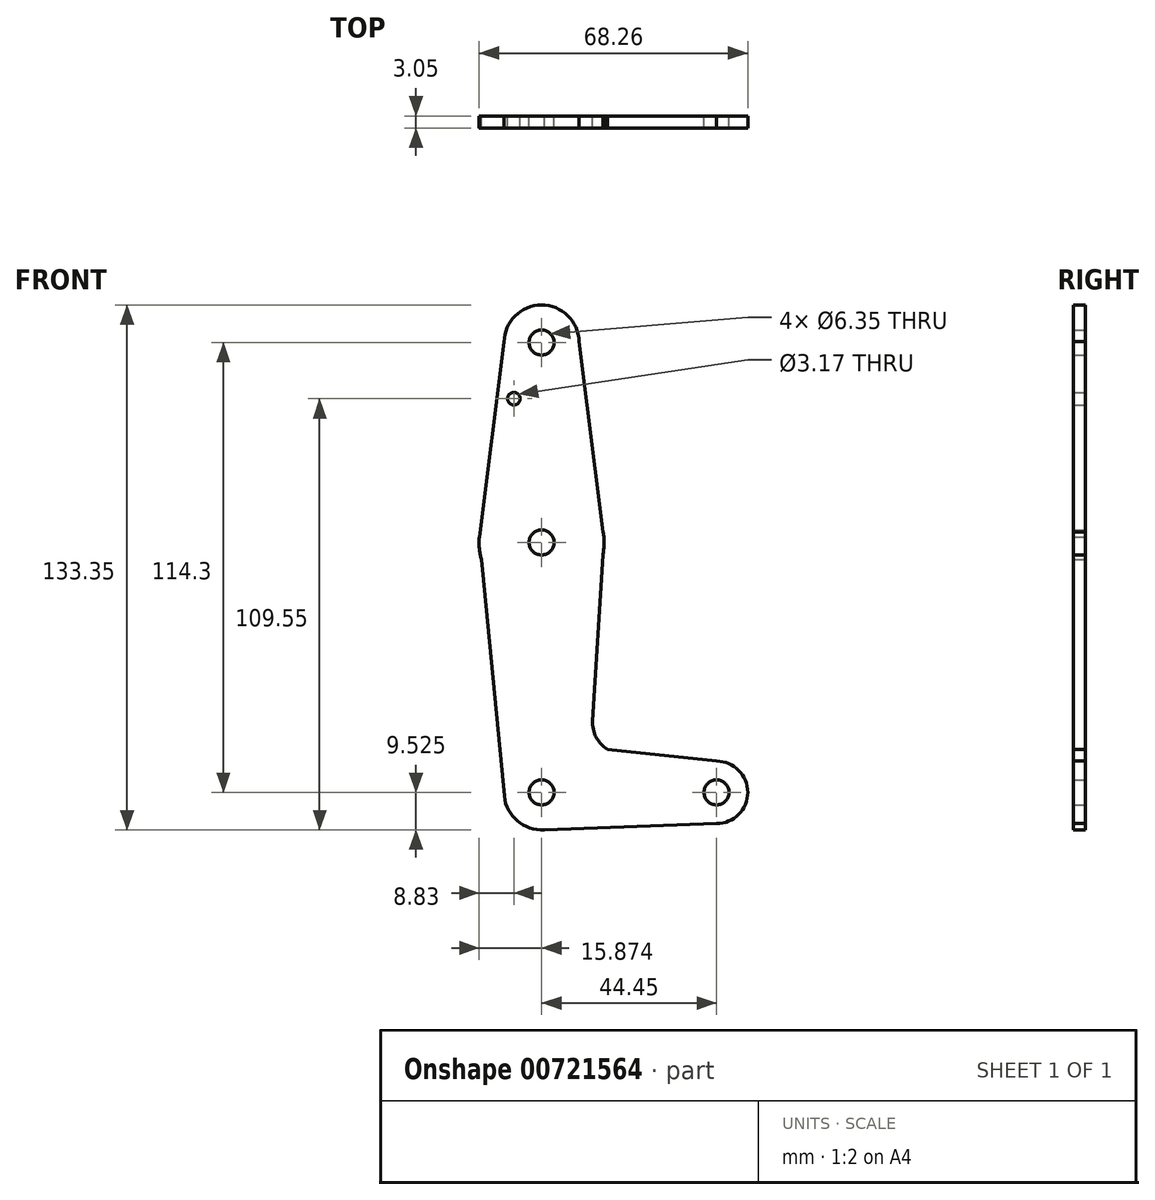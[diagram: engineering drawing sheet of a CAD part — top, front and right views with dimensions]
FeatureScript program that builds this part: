
annotation { "Feature Type Name" : "Feature", "Feature Type Description" : "" }
export const myFeature = defineFeature(function(context is Context, id is Id, definition is map)
    precondition{}
    {
        {
            var Q0;
            Q0=qCreatedBy(makeId("Front.planeOp"),FACE);
            var sketch = newSketch(context, id + "F0", { "sketchPlane" : qUnion([Q0])});
            skCircle(sketch, "E0", {"center": v(-20.1, -1.33) * mm, "radius": 15.88 * mm});
            skLineSegment(sketch, "E1", {"start": v(-20.1, -1.33) * mm, "end": v(-20.1, 49.47) * mm, "construction": true});
            skCircle(sketch, "E2", {"center": v(-20.1, 49.47) * mm, "radius": 9.53 * mm});
            skLineSegment(sketch, "E3", {"start": v(-20.1, -1.33) * mm, "end": v(-20.1, -64.83) * mm, "construction": true});
            skCircle(sketch, "E4", {"center": v(-20.1, -64.83) * mm, "radius": 9.53 * mm});
            skLineSegment(sketch, "E5", {"start": v(-29.63, 49.6) * mm, "end": v(-35.94, 0) * mm});
            skLineSegment(sketch, "E6", {"start": v(-35.94, 0) * mm, "end": v(-35.93, 0) * mm});
            skLineSegment(sketch, "E7", {"start": v(-4.29, 0) * mm, "end": v(-10.58, 49.7) * mm});
            skLineSegment(sketch, "E8", {"start": v(-35.93, 0) * mm, "end": v(-29.59, -65.74) * mm});
            skLineSegment(sketch, "E9", {"start": v(-4.29, 0) * mm, "end": v(-7.14, -46.62) * mm});
            skCircle(sketch, "E10.0", {"center": v(-20.1, 49.47) * mm, "radius": 3.17 * mm});
            skCircle(sketch, "E11", {"center": v(-27.15, 35.2) * mm, "radius": 1.59 * mm});
            skLineSegment(sketch, "E12", {"start": v(-20.1, -64.83) * mm, "end": v(24.34, -64.83) * mm, "construction": true});
            skCircle(sketch, "E13", {"center": v(24.34, -64.83) * mm, "radius": 7.94 * mm});
            skArc(sketch, "E14", {"start": v(-7.14, -46.62) * mm, "mid": v(-6.26, -50.78) * mm, "end": v(-3.37, -53.89) * mm});
            skLineSegment(sketch, "E15", {"start": v(-3.37, -53.89) * mm, "end": v(24.34, -56.89) * mm});
            skLineSegment(sketch, "E16", {"start": v(24.34, -72.76) * mm, "end": v(-20.11, -74.35) * mm});
            skCircle(sketch, "E17", {"center": v(-20.1, -1.33) * mm, "radius": 3.18 * mm});
            skCircle(sketch, "E18", {"center": v(24.34, -64.83) * mm, "radius": 3.18 * mm});
            skCircle(sketch, "E19", {"center": v(-20.1, -64.83) * mm, "radius": 3.18 * mm});
            skSolve(sketch);
        }
        {
            var Q0;
            Q0 = qSketchRegion(id + "F0", true);
            extrude(context, id + "F1", {"entities" : qUnion([Q0]), "depth" : 3.05 * mm, "offsetDistance" : 25.4 * mm});
        }
    });
